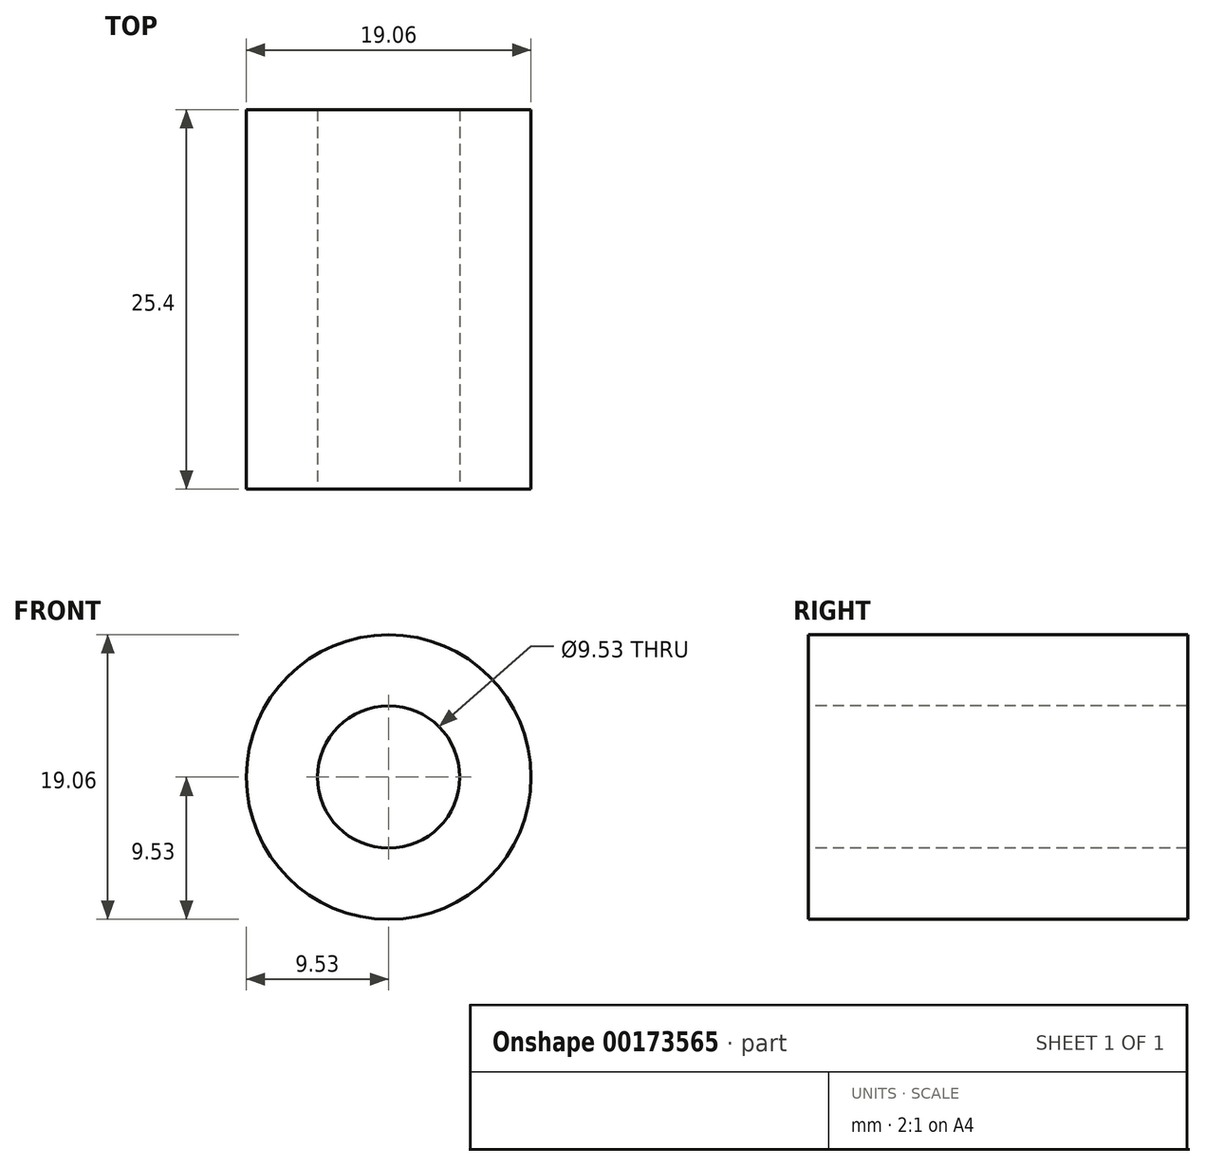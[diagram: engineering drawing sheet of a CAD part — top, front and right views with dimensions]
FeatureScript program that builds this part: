
annotation { "Feature Type Name" : "Feature", "Feature Type Description" : "" }
export const myFeature = defineFeature(function(context is Context, id is Id, definition is map)
    precondition{}
    {
        {
            var Q0;
            Q0=qCreatedBy(makeId("Front.planeOp"),FACE);
            var sketch = newSketch(context, id + "F0", { "sketchPlane" : qUnion([Q0])});
            skCircle(sketch, "E0", {"center": v(0, 0) * mm, "radius": 9.53 * mm});
            skSolve(sketch);
        }
        {
            var Q0;
            Q0 = qSketchRegion(id + "F0", true);
            extrude(context, id + "F1", {"entities" : qUnion([Q0]), "endBound" : BoundingType.SYMMETRIC, "depth" : 25.4 * mm});
        }
        {
            var Q0;
            Q0=makeQuery(id+"F1.opExtrude","CAP_FACE",FACE,{"disambiguationData":[OSD([sQuery(id+"F0.wireOp",EDGE,"E0")])],"isStart":false});
            var sketch = newSketch(context, id + "F2", { "sketchPlane" : qUnion([Q0])});
            skLineSegment(sketch, "E1.bottom", {"start": v(-4.76, 4.76) * mm, "end": v(4.76, 4.76) * mm});
            skLineSegment(sketch, "E1.top", {"start": v(-4.76, -4.76) * mm, "end": v(4.76, -4.76) * mm});
            skLineSegment(sketch, "E1.left", {"start": v(-4.76, 4.76) * mm, "end": v(-4.76, -4.76) * mm});
            skLineSegment(sketch, "E1.right", {"start": v(4.76, 4.76) * mm, "end": v(4.76, -4.76) * mm});
            skCircle(sketch, "E2", {"center": v(0, 0) * mm, "radius": 4.76 * mm});
            skSolve(sketch);
        }
        {
            var Q0;
            {var subQ0=sQuery(id+"F2.wireOp",EDGE,"E2");var subQ1=makeQuery(id+"F2.imprint","INTERSECT",VERTEX,{"derivedFrom":[sQuery(id+"F2.wireOp",EDGE,"E1.bottom"),subQ0]});Q0=makeQuery(id+"F2.imprint","IMPRINT",FACE,{"disambiguationData":[TD([[makeQuery(id+"F2.imprint","IMPRINT",EDGE,{"disambiguationData":[TD([[subQ1,1.0]])],"derivedFrom":subQ0}),1.0]])]});}
            extrude(context, id + "F3", {"entities" : qUnion([Q0]), "operationType" : NewBodyOperationType.REMOVE, "endBound" : BoundingType.THROUGH_ALL, "oppositeDirection" : true, "depth" : 25.4 * mm});
        }
    });
